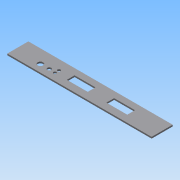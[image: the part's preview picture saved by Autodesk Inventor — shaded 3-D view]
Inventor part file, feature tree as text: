
AUTODESK INVENTOR PART (.ipt)
format: ipt  version: 2013 (Build 170138000, 138)  size: 112,640 bytes
history: native  units: mm
features: extrude x2, sketch x2
ambient origin geometry x8: Origin, YZ Plane, XZ Plane, XY Plane, X Axis, Y Axis, Z Axis, Center Point
bodies: Solid1 (feature_tree)
feature tree (4):
  extrude  "Extrusion1"  Depth=26.9mm
  extrude  "Extrusion3"  Depth=7.0mm
  sketch  "Sketch1"  dims[d0=184.2mm d2=26.9mm]
  sketch  "Sketch5"  dims[d3=1.9mm d4=0.0mm d56=7.0mm d58=5.0mm d59=32.5mm d60=43.75mm d61=9.75mm d62=9.75mm d63=3.8mm d64=3.8mm d65=51.55mm d66=51.55mm d67=9.25mm d68=14.45mm d69=26.6mm d70=26.6mm d71=9.9mm d72=9.9mm d73=9.0mm d74=9.0mm d75=117.15mm d76=66.7mm d77=2.0mm d78=0.0mm]
